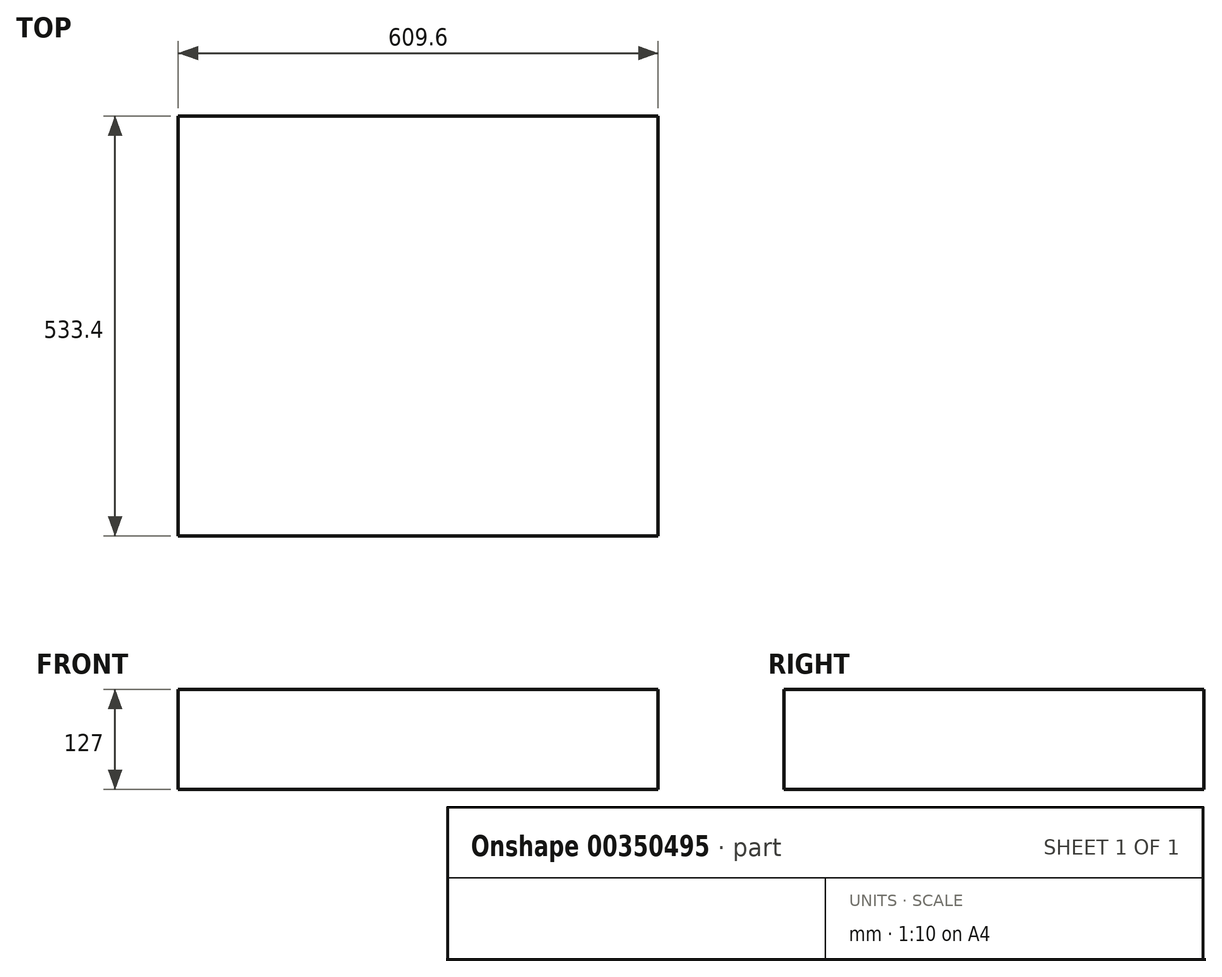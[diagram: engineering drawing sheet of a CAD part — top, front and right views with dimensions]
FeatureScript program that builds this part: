
annotation { "Feature Type Name" : "Feature", "Feature Type Description" : "" }
export const myFeature = defineFeature(function(context is Context, id is Id, definition is map)
    precondition{}
    {
        {
            var Q0;
            Q0=qCreatedBy(makeId("Top.planeOp"),FACE);
            var sketch = newSketch(context, id + "F0", { "sketchPlane" : qUnion([Q0])});
            skLineSegment(sketch, "E0.bottom", {"start": v(-351.43, 231.44) * mm, "end": v(258.17, 231.44) * mm});
            skLineSegment(sketch, "E0.top", {"start": v(-351.43, -301.96) * mm, "end": v(258.17, -301.96) * mm});
            skLineSegment(sketch, "E0.left", {"start": v(-351.43, 231.44) * mm, "end": v(-351.43, -301.96) * mm});
            skLineSegment(sketch, "E0.right", {"start": v(258.17, 231.44) * mm, "end": v(258.17, -301.96) * mm});
            skSolve(sketch);
        }
        {
            var Q0;
            Q0 = qSketchRegion(id + "F0", true);
            extrude(context, id + "F1", {"entities" : qUnion([Q0]), "depth" : 127 * mm});
        }
    });
